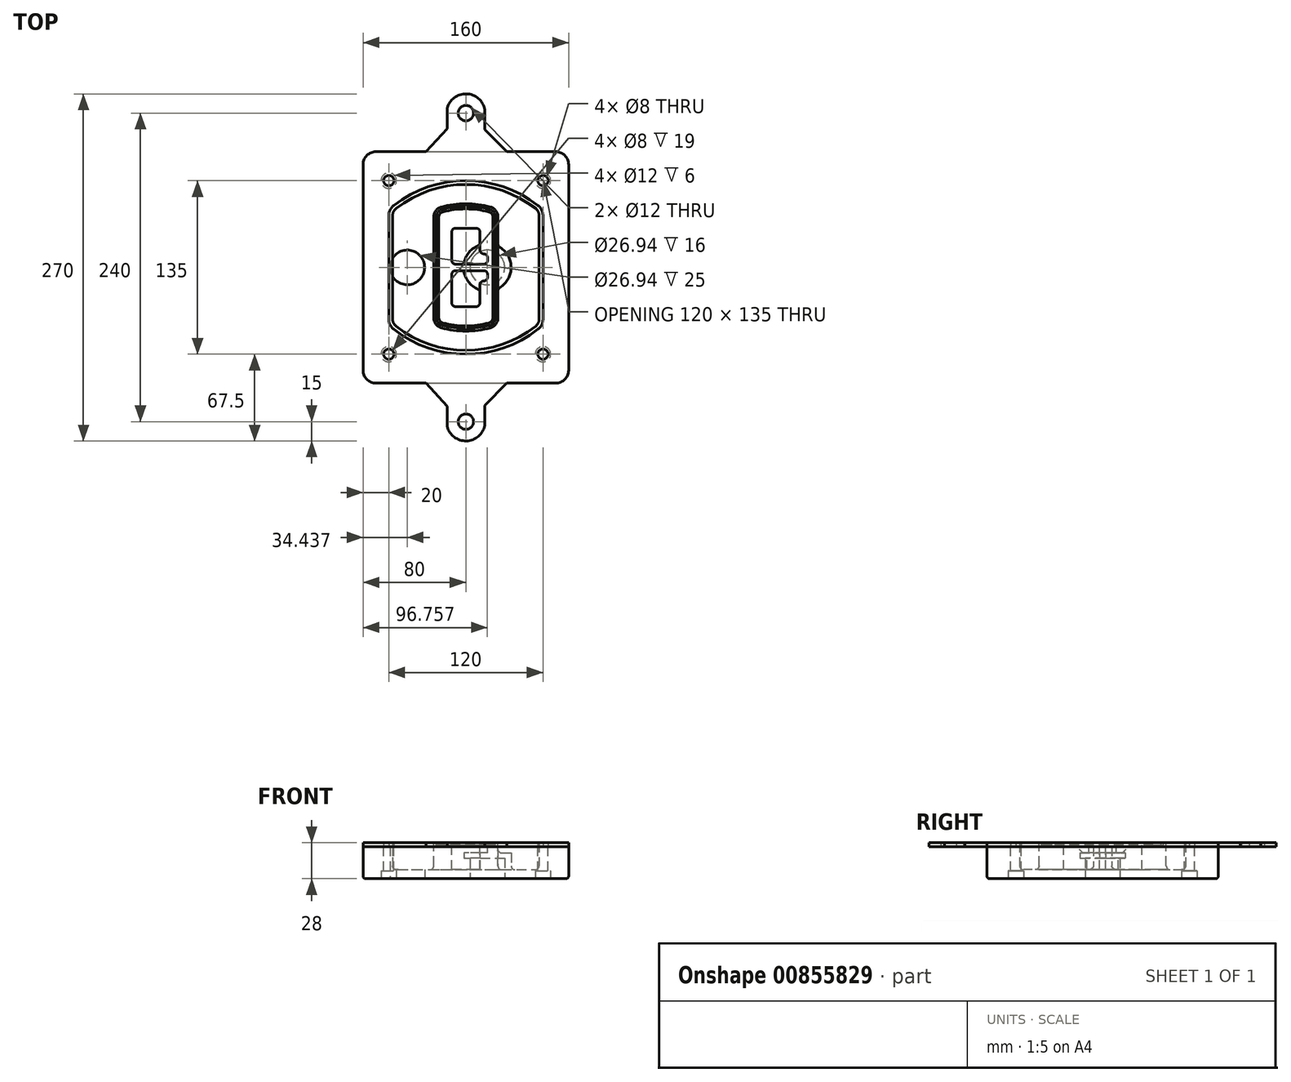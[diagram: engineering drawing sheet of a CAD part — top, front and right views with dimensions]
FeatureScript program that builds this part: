
annotation { "Feature Type Name" : "Feature", "Feature Type Description" : "" }
export const myFeature = defineFeature(function(context is Context, id is Id, definition is map)
    precondition{}
    {
        {
            var Q0;
            Q0=qCreatedBy(makeId("Top.planeOp"),FACE);
            var sketch = newSketch(context, id + "F0", { "sketchPlane" : qUnion([Q0])});
            skPoint(sketch, "E0.rect.middle", {"position": v(0, 0) * mm});
            skLineSegment(sketch, "E1.bottom", {"start": v(-70, -90) * mm, "end": v(70, -90) * mm});
            skLineSegment(sketch, "E1.top", {"start": v(-70, 90) * mm, "end": v(70, 90) * mm});
            skLineSegment(sketch, "E1.left", {"start": v(-80, -80) * mm, "end": v(-80, 80) * mm});
            skLineSegment(sketch, "E1.right", {"start": v(80, -80) * mm, "end": v(80, 80) * mm});
            skLineSegment(sketch, "E2", {"start": v(-80, 90) * mm, "end": v(80, -90) * mm, "construction": true});
            skLineSegment(sketch, "E3", {"start": v(80, 90) * mm, "end": v(-80, -90) * mm, "construction": true});
            skCircle(sketch, "E4", {"center": v(-60, 67.5) * mm, "radius": 4 * mm});
            skCircle(sketch, "E5", {"center": v(60, 67.5) * mm, "radius": 4 * mm});
            skCircle(sketch, "E6", {"center": v(60, -67.5) * mm, "radius": 4 * mm});
            skCircle(sketch, "E7", {"center": v(-60, -67.5) * mm, "radius": 4 * mm});
            skLineSegment(sketch, "E8", {"start": v(-60, 67.5) * mm, "end": v(60, 67.5) * mm, "construction": true});
            skLineSegment(sketch, "E9", {"start": v(60, 67.5) * mm, "end": v(60, -67.5) * mm, "construction": true});
            skLineSegment(sketch, "E10", {"start": v(60, -67.5) * mm, "end": v(-60, -67.5) * mm, "construction": true});
            skLineSegment(sketch, "E11", {"start": v(-60, -67.5) * mm, "end": v(-60, 67.5) * mm, "construction": true});
            skLineSegment(sketch, "E12", {"start": v(-60, 40.3) * mm, "end": v(-60, -40.3) * mm});
            skLineSegment(sketch, "E13", {"start": v(60, 40.3) * mm, "end": v(60, -40.3) * mm});
            skArc(sketch, "E14", {"start": v(56.15, 48.18) * mm, "mid": v(0, 67.5) * mm, "end": v(-56.15, 48.18) * mm});
            skArc(sketch, "E15", {"start": v(-56.15, -48.18) * mm, "mid": v(0, -67.5) * mm, "end": v(56.15, -48.18) * mm});
            skLineSegment(sketch, "E16", {"start": v(-60, 0) * mm, "end": v(60, 0) * mm, "construction": true});
            skPoint(sketch, "E17.visualSharp", {"position": v(-60, -45) * mm});
            skArc(sketch, "E17.filletArc", {"start": v(-60, -40.3) * mm, "mid": v(-58.99, -44.68) * mm, "end": v(-56.15, -48.18) * mm});
            skPoint(sketch, "E18.visualSharp", {"position": v(-60, 45) * mm});
            skArc(sketch, "E18.filletArc", {"start": v(-56.15, 48.18) * mm, "mid": v(-58.99, 44.68) * mm, "end": v(-60, 40.3) * mm});
            skPoint(sketch, "E19.visualSharp", {"position": v(60, 45) * mm});
            skArc(sketch, "E19.filletArc", {"start": v(60, 40.3) * mm, "mid": v(58.99, 44.68) * mm, "end": v(56.15, 48.18) * mm});
            skPoint(sketch, "E20.visualSharp", {"position": v(60, -45) * mm});
            skArc(sketch, "E20.filletArc", {"start": v(56.15, -48.18) * mm, "mid": v(58.99, -44.68) * mm, "end": v(60, -40.3) * mm});
            skPoint(sketch, "E21.visualSharp", {"position": v(-80, 90) * mm});
            skArc(sketch, "E21.filletArc", {"start": v(-70, 90) * mm, "mid": v(-77.07, 87.07) * mm, "end": v(-80, 80) * mm});
            skPoint(sketch, "E22.visualSharp", {"position": v(80, 90) * mm});
            skArc(sketch, "E22.filletArc", {"start": v(80, 80) * mm, "mid": v(77.07, 87.07) * mm, "end": v(70, 90) * mm});
            skPoint(sketch, "E23.visualSharp", {"position": v(80, -90) * mm});
            skArc(sketch, "E23.filletArc", {"start": v(70, -90) * mm, "mid": v(77.07, -87.07) * mm, "end": v(80, -80) * mm});
            skPoint(sketch, "E24.visualSharp", {"position": v(-80, -90) * mm});
            skArc(sketch, "E24.filletArc", {"start": v(-80, -80) * mm, "mid": v(-77.07, -87.07) * mm, "end": v(-70, -90) * mm});
            skArc(sketch, "E25.0", {"start": v(57, 40.3) * mm, "mid": v(56.3, 43.36) * mm, "end": v(54.3, 45.81) * mm});
            skLineSegment(sketch, "E25.1", {"start": v(57, 40.3) * mm, "end": v(57, -40.3) * mm});
            skArc(sketch, "E25.2", {"start": v(54.3, -45.81) * mm, "mid": v(56.3, -43.36) * mm, "end": v(57, -40.3) * mm});
            skArc(sketch, "E25.3", {"start": v(-54.3, -45.81) * mm, "mid": v(0, -64.5) * mm, "end": v(54.3, -45.81) * mm});
            skArc(sketch, "E25.4", {"start": v(-57, -40.3) * mm, "mid": v(-56.3, -43.36) * mm, "end": v(-54.3, -45.81) * mm});
            skArc(sketch, "E25.5", {"start": v(54.3, 45.81) * mm, "mid": v(0, 64.5) * mm, "end": v(-54.3, 45.81) * mm});
            skLineSegment(sketch, "E25.6", {"start": v(-57, 40.3) * mm, "end": v(-57, -40.3) * mm});
            skArc(sketch, "E25.7", {"start": v(-54.3, 45.81) * mm, "mid": v(-56.3, 43.36) * mm, "end": v(-57, 40.3) * mm});
            skArc(sketch, "E26.0", {"start": v(-58.62, 51.33) * mm, "mid": v(-62.58, 46.43) * mm, "end": v(-64, 40.3) * mm});
            skArc(sketch, "E26.1", {"start": v(58.62, 51.33) * mm, "mid": v(0, 71.5) * mm, "end": v(-58.62, 51.33) * mm});
            skArc(sketch, "E26.2", {"start": v(64, 40.3) * mm, "mid": v(62.58, 46.43) * mm, "end": v(58.62, 51.33) * mm});
            skLineSegment(sketch, "E26.3", {"start": v(64, 40.3) * mm, "end": v(64, -40.3) * mm});
            skArc(sketch, "E26.4", {"start": v(58.62, -51.33) * mm, "mid": v(62.58, -46.43) * mm, "end": v(64, -40.3) * mm});
            skLineSegment(sketch, "E26.5", {"start": v(-64, 40.3) * mm, "end": v(-64, -40.3) * mm});
            skArc(sketch, "E26.6", {"start": v(-58.62, -51.33) * mm, "mid": v(0, -71.5) * mm, "end": v(58.62, -51.33) * mm});
            skArc(sketch, "E26.7", {"start": v(-64, -40.3) * mm, "mid": v(-62.58, -46.43) * mm, "end": v(-58.62, -51.33) * mm});
            skSolve(sketch);
        }
        {
            var Q0;
            Q0=makeQuery(id+"F0.imprint","IMPRINT",FACE,{"disambiguationData":[TD([[makeQuery(id+"F0.imprint","IMPRINT",EDGE,{"derivedFrom":sQuery(id+"F0.wireOp",EDGE,"E1.bottom")}),1.0]])]});
            var Q1;
            Q1=makeQuery(id+"F0.imprint","IMPRINT",FACE,{"disambiguationData":[TD([[makeQuery(id+"F0.imprint","IMPRINT",EDGE,{"derivedFrom":sQuery(id+"F0.wireOp",EDGE,"E12")}),1.0]])]});
            var Q2;
            Q2=makeQuery(id+"F0.imprint","IMPRINT",FACE,{"disambiguationData":[TD([[makeQuery(id+"F0.imprint","IMPRINT",EDGE,{"derivedFrom":sQuery(id+"F0.wireOp",EDGE,"E25.0")}),1.0]])]});
            var Q3;
            Q3=makeQuery(id+"F0.imprint","IMPRINT",FACE,{"disambiguationData":[TD([[makeQuery(id+"F0.imprint","IMPRINT",EDGE,{"derivedFrom":sQuery(id+"F0.wireOp",EDGE,"E12")}),-1.0]])]});
            extrude(context, id + "F1", {"entities" : qUnion([Q0, Q1, Q2, Q3]), "oppositeDirection" : true, "depth" : 25 * mm});
        }
        {
            var Q0;
            Q0=makeQuery(id+"F0.imprint","IMPRINT",FACE,{"disambiguationData":[TD([[makeQuery(id+"F0.imprint","IMPRINT",EDGE,{"derivedFrom":sQuery(id+"F0.wireOp",EDGE,"E12")}),1.0]])]});
            extrude(context, id + "F2", {"entities" : qUnion([Q0]), "operationType" : NewBodyOperationType.ADD, "depth" : 3 * mm});
        }
        {
            var Q0;
            Q0=makeQuery(id+"F0.imprint","IMPRINT",FACE,{"disambiguationData":[TD([[makeQuery(id+"F0.imprint","IMPRINT",EDGE,{"derivedFrom":sQuery(id+"F0.wireOp",EDGE,"E25.0")}),1.0]])]});
            extrude(context, id + "F3", {"entities" : qUnion([Q0]), "operationType" : NewBodyOperationType.REMOVE, "oppositeDirection" : true, "depth" : 18 * mm});
        }
        {
            var Q0;
            Q0=makeQuery(id+"F2.opExtrude","CAP_FACE",FACE,{"disambiguationData":[OSD([sQuery(id+"F0.wireOp",EDGE,"E12"),sQuery(id+"F0.wireOp",EDGE,"E13"),sQuery(id+"F0.wireOp",EDGE,"E14"),sQuery(id+"F0.wireOp",EDGE,"E15"),sQuery(id+"F0.wireOp",EDGE,"E17.filletArc"),sQuery(id+"F0.wireOp",EDGE,"E18.filletArc"),sQuery(id+"F0.wireOp",EDGE,"E19.filletArc"),sQuery(id+"F0.wireOp",EDGE,"E20.filletArc"),sQuery(id+"F0.wireOp",EDGE,"E25.0"),sQuery(id+"F0.wireOp",EDGE,"E25.1"),sQuery(id+"F0.wireOp",EDGE,"E25.2"),sQuery(id+"F0.wireOp",EDGE,"E25.3"),sQuery(id+"F0.wireOp",EDGE,"E25.4"),sQuery(id+"F0.wireOp",EDGE,"E25.5"),sQuery(id+"F0.wireOp",EDGE,"E25.6"),sQuery(id+"F0.wireOp",EDGE,"E25.7")])],"isStart":false});
            var sketch = newSketch(context, id + "F4", { "sketchPlane" : qUnion([Q0])});
            skArc(sketch, "E27.0", {"start": v(-19.08, -46.97) * mm, "mid": v(0, -49.5) * mm, "end": v(19.08, -46.97) * mm});
            skArc(sketch, "E28.0", {"start": v(19.08, 46.97) * mm, "mid": v(0, 49.5) * mm, "end": v(-19.08, 46.97) * mm});
            skLineSegment(sketch, "E29", {"start": v(-25, 39.25) * mm, "end": v(-25, -39.25) * mm});
            skLineSegment(sketch, "E30", {"start": v(25, 39.25) * mm, "end": v(25, -39.25) * mm});
            skLineSegment(sketch, "E31", {"start": v(-25, 45.1) * mm, "end": v(25, 45.1) * mm, "construction": true});
            skLineSegment(sketch, "E32", {"start": v(-25, -45.1) * mm, "end": v(25, -45.1) * mm, "construction": true});
            skPoint(sketch, "E33.visualSharp", {"position": v(-25, 45.1) * mm});
            skArc(sketch, "E33.filletArc", {"start": v(-19.08, 46.97) * mm, "mid": v(-23.35, 44.11) * mm, "end": v(-25, 39.25) * mm});
            skPoint(sketch, "E34.visualSharp", {"position": v(25, 45.1) * mm});
            skArc(sketch, "E34.filletArc", {"start": v(25, 39.25) * mm, "mid": v(23.35, 44.11) * mm, "end": v(19.08, 46.97) * mm});
            skPoint(sketch, "E35.visualSharp", {"position": v(25, -45.1) * mm});
            skArc(sketch, "E35.filletArc", {"start": v(19.08, -46.97) * mm, "mid": v(23.35, -44.11) * mm, "end": v(25, -39.25) * mm});
            skPoint(sketch, "E36.visualSharp", {"position": v(-25, -45.1) * mm});
            skArc(sketch, "E36.filletArc", {"start": v(-25, -39.25) * mm, "mid": v(-23.35, -44.11) * mm, "end": v(-19.08, -46.97) * mm});
            skArc(sketch, "E37.0", {"start": v(54.3, 45.81) * mm, "mid": v(0, 64.5) * mm, "end": v(-54.3, 45.81) * mm});
            skArc(sketch, "E37.1", {"start": v(-54.3, 45.81) * mm, "mid": v(-56.3, 43.36) * mm, "end": v(-57, 40.3) * mm});
            skLineSegment(sketch, "E37.2", {"start": v(-57, 40.3) * mm, "end": v(-57, -40.3) * mm});
            skArc(sketch, "E37.3", {"start": v(-57, -40.3) * mm, "mid": v(-56.3, -43.36) * mm, "end": v(-54.3, -45.81) * mm});
            skArc(sketch, "E37.4", {"start": v(-54.3, -45.81) * mm, "mid": v(0, -64.5) * mm, "end": v(54.3, -45.81) * mm});
            skArc(sketch, "E37.5", {"start": v(54.3, -45.81) * mm, "mid": v(56.3, -43.36) * mm, "end": v(57, -40.3) * mm});
            skLineSegment(sketch, "E37.6", {"start": v(57, 40.3) * mm, "end": v(57, -40.3) * mm});
            skArc(sketch, "E37.7", {"start": v(57, 40.3) * mm, "mid": v(56.3, 43.36) * mm, "end": v(54.3, 45.81) * mm});
            skLineSegment(sketch, "E38.0", {"start": v(23, 39.25) * mm, "end": v(23, -39.25) * mm});
            skArc(sketch, "E38.1", {"start": v(18.56, -45.04) * mm, "mid": v(21.76, -42.9) * mm, "end": v(23, -39.25) * mm});
            skArc(sketch, "E38.2", {"start": v(-18.56, -45.04) * mm, "mid": v(0, -47.5) * mm, "end": v(18.56, -45.04) * mm});
            skArc(sketch, "E38.3", {"start": v(-23, -39.25) * mm, "mid": v(-21.76, -42.9) * mm, "end": v(-18.56, -45.04) * mm});
            skLineSegment(sketch, "E38.4", {"start": v(-23, 39.25) * mm, "end": v(-23, -39.25) * mm});
            skArc(sketch, "E38.5", {"start": v(23, 39.25) * mm, "mid": v(21.76, 42.9) * mm, "end": v(18.56, 45.04) * mm});
            skArc(sketch, "E38.6", {"start": v(-18.56, 45.04) * mm, "mid": v(-21.76, 42.9) * mm, "end": v(-23, 39.25) * mm});
            skArc(sketch, "E38.7", {"start": v(18.56, 45.04) * mm, "mid": v(0, 47.5) * mm, "end": v(-18.56, 45.04) * mm});
            skArc(sketch, "E39.0", {"start": v(21, 39.25) * mm, "mid": v(20.18, 41.68) * mm, "end": v(18.04, 43.1) * mm});
            skLineSegment(sketch, "E39.1", {"start": v(21, 39.25) * mm, "end": v(21, -39.25) * mm});
            skArc(sketch, "E39.2", {"start": v(18.04, -43.1) * mm, "mid": v(20.18, -41.68) * mm, "end": v(21, -39.25) * mm});
            skArc(sketch, "E39.3", {"start": v(-18.04, -43.1) * mm, "mid": v(0, -45.5) * mm, "end": v(18.04, -43.1) * mm});
            skArc(sketch, "E39.4", {"start": v(-21, -39.25) * mm, "mid": v(-20.18, -41.68) * mm, "end": v(-18.04, -43.1) * mm});
            skArc(sketch, "E39.5", {"start": v(18.04, 43.1) * mm, "mid": v(0, 45.5) * mm, "end": v(-18.04, 43.1) * mm});
            skLineSegment(sketch, "E39.6", {"start": v(-21, 39.25) * mm, "end": v(-21, -39.25) * mm});
            skArc(sketch, "E39.7", {"start": v(-18.04, 43.1) * mm, "mid": v(-20.18, 41.68) * mm, "end": v(-21, 39.25) * mm});
            skLineSegment(sketch, "E40", {"start": v(-25, 0) * mm, "end": v(25, 0) * mm, "construction": true});
            skLineSegment(sketch, "E41", {"start": v(-11, 5.5) * mm, "end": v(-11, 27.5) * mm});
            skLineSegment(sketch, "E42", {"start": v(-8, 30.5) * mm, "end": v(8, 30.5) * mm});
            skLineSegment(sketch, "E43", {"start": v(11, 27.5) * mm, "end": v(11, 13.5) * mm});
            skLineSegment(sketch, "E44", {"start": v(14, 10.5) * mm, "end": v(14, 10.5) * mm});
            skLineSegment(sketch, "E45", {"start": v(17, 7.5) * mm, "end": v(17, 5.5) * mm});
            skLineSegment(sketch, "E46", {"start": v(14, 2.5) * mm, "end": v(-8, 2.5) * mm});
            skPoint(sketch, "E47.visualSharp", {"position": v(-11, 30.5) * mm});
            skArc(sketch, "E47.filletArc", {"start": v(-8, 30.5) * mm, "mid": v(-10.12, 29.62) * mm, "end": v(-11, 27.5) * mm});
            skPoint(sketch, "E48.visualSharp", {"position": v(11, 30.5) * mm});
            skArc(sketch, "E48.filletArc", {"start": v(11, 27.5) * mm, "mid": v(10.12, 29.62) * mm, "end": v(8, 30.5) * mm});
            skPoint(sketch, "E49.visualSharp", {"position": v(11, 10.5) * mm});
            skArc(sketch, "E49.filletArc", {"start": v(11, 13.5) * mm, "mid": v(11.88, 11.38) * mm, "end": v(14, 10.5) * mm});
            skPoint(sketch, "E50.visualSharp", {"position": v(17, 10.5) * mm});
            skArc(sketch, "E50.filletArc", {"start": v(17, 7.5) * mm, "mid": v(16.12, 9.62) * mm, "end": v(14, 10.5) * mm});
            skPoint(sketch, "E51.visualSharp", {"position": v(17, 2.5) * mm});
            skArc(sketch, "E51.filletArc", {"start": v(14, 2.5) * mm, "mid": v(16.12, 3.38) * mm, "end": v(17, 5.5) * mm});
            skPoint(sketch, "E52.visualSharp", {"position": v(-11, 2.5) * mm});
            skArc(sketch, "E52.filletArc", {"start": v(-11, 5.5) * mm, "mid": v(-10.12, 3.38) * mm, "end": v(-8, 2.5) * mm});
            skLineSegment(sketch, "E53.0.MirrorCS", {"start": v(14, -2.5) * mm, "end": v(-8, -2.5) * mm});
            skArc(sketch, "E54.0.MirrorCS", {"start": v(-11, -5.5) * mm, "mid": v(-10.12, -3.38) * mm, "end": v(-8, -2.5) * mm});
            skLineSegment(sketch, "E55.0.MirrorCS", {"start": v(-11, -5.5) * mm, "end": v(-11, -27.5) * mm});
            skArc(sketch, "E56.0.MirrorCS", {"start": v(-8, -30.5) * mm, "mid": v(-10.12, -29.62) * mm, "end": v(-11, -27.5) * mm});
            skLineSegment(sketch, "E57.0.MirrorCS", {"start": v(-8, -30.5) * mm, "end": v(8, -30.5) * mm});
            skArc(sketch, "E58.0.MirrorCS", {"start": v(11, -27.5) * mm, "mid": v(10.12, -29.62) * mm, "end": v(8, -30.5) * mm});
            skLineSegment(sketch, "E59.0.MirrorCS", {"start": v(11, -27.5) * mm, "end": v(11, -13.5) * mm});
            skArc(sketch, "E60.0.MirrorCS", {"start": v(11, -13.5) * mm, "mid": v(11.88, -11.38) * mm, "end": v(14, -10.5) * mm});
            skArc(sketch, "E61.0.MirrorCS", {"start": v(17, -7.5) * mm, "mid": v(16.12, -9.62) * mm, "end": v(14, -10.5) * mm});
            skLineSegment(sketch, "E62.0.MirrorCS", {"start": v(17, -7.5) * mm, "end": v(17, -5.5) * mm});
            skArc(sketch, "E63.0.MirrorCS", {"start": v(14, -2.5) * mm, "mid": v(16.12, -3.38) * mm, "end": v(17, -5.5) * mm});
            skSolve(sketch);
        }
        {
            var Q0;
            Q0=makeQuery(id+"F4.imprint","IMPRINT",FACE,{"disambiguationData":[TD([[makeQuery(id+"F4.imprint","IMPRINT",EDGE,{"derivedFrom":sQuery(id+"F4.wireOp",EDGE,"E27.0")}),1.0]])]});
            var Q1;
            Q1=makeQuery(id+"F4.imprint","IMPRINT",FACE,{"disambiguationData":[TD([[makeQuery(id+"F4.imprint","IMPRINT",EDGE,{"derivedFrom":sQuery(id+"F4.wireOp",EDGE,"E38.0")}),-1.0]])]});
            var Q2;
            Q2=makeQuery(id+"F4.imprint","IMPRINT",FACE,{"disambiguationData":[TD([[makeQuery(id+"F4.imprint","IMPRINT",EDGE,{"derivedFrom":sQuery(id+"F4.wireOp",EDGE,"E39.0")}),1.0]])]});
            extrude(context, id + "F5", {"entities" : qUnion([Q0, Q1, Q2]), "operationType" : NewBodyOperationType.ADD, "endBound" : BoundingType.UP_TO_NEXT, "oppositeDirection" : true, "depth" : 25 * mm});
        }
        {
            var Q0;
            Q0=makeQuery(id+"F4.imprint","IMPRINT",FACE,{"disambiguationData":[TD([[makeQuery(id+"F4.imprint","IMPRINT",EDGE,{"derivedFrom":sQuery(id+"F4.wireOp",EDGE,"E38.0")}),-1.0]])]});
            extrude(context, id + "F6", {"entities" : qUnion([Q0]), "operationType" : NewBodyOperationType.REMOVE, "oppositeDirection" : true, "depth" : 2 * mm});
        }
        {
            var Q0;
            Q0=makeQuery(id+"F1.opExtrude","CAP_FACE",FACE,{"disambiguationData":[OSD([sQuery(id+"F0.wireOp",EDGE,"E1.bottom"),sQuery(id+"F0.wireOp",EDGE,"E1.top"),sQuery(id+"F0.wireOp",EDGE,"E1.left"),sQuery(id+"F0.wireOp",EDGE,"E1.right"),sQuery(id+"F0.wireOp",EDGE,"E4"),sQuery(id+"F0.wireOp",EDGE,"E5"),sQuery(id+"F0.wireOp",EDGE,"E6"),sQuery(id+"F0.wireOp",EDGE,"E7"),sQuery(id+"F0.wireOp",EDGE,"E21.filletArc"),sQuery(id+"F0.wireOp",EDGE,"E22.filletArc"),sQuery(id+"F0.wireOp",EDGE,"E23.filletArc"),sQuery(id+"F0.wireOp",EDGE,"E24.filletArc")])],"isStart":false});
            var sketch = newSketch(context, id + "F7", { "sketchPlane" : qUnion([Q0])});
            skCircle(sketch, "E64", {"center": v(16.76, 0) * mm, "radius": 13.47 * mm});
            skCircle(sketch, "E65", {"center": v(-45.56, 0) * mm, "radius": 13.47 * mm});
            skLineSegment(sketch, "E66", {"start": v(80, 0) * mm, "end": v(-80, 0) * mm});
            skCircle(sketch, "E67", {"center": v(16.76, 0) * mm, "radius": 18.47 * mm});
            skCircle(sketch, "E68", {"center": v(60, -67.5) * mm, "radius": 6 * mm});
            skCircle(sketch, "E69", {"center": v(-60, -67.5) * mm, "radius": 6 * mm});
            skCircle(sketch, "E70", {"center": v(-60, 67.5) * mm, "radius": 6 * mm});
            skCircle(sketch, "E71", {"center": v(60, 67.5) * mm, "radius": 6 * mm});
            skSolve(sketch);
        }
        {
            var Q0;
            {var subQ1=sQuery(id+"F7.wireOp",EDGE,"E66");var subQ4=sQuery(id+"F7.wireOp",EDGE,"E64");var subQ6=makeQuery(id+"F7.imprint","INTERSECT",VERTEX,{"disambiguationData":[OD(0.0)],"derivedFrom":[subQ4,subQ1]});Q0=makeQuery(id+"F7.imprint","IMPRINT",FACE,{"disambiguationData":[TD([[makeQuery(id+"F7.imprint","IMPRINT",EDGE,{"disambiguationData":[TD([[subQ6,-1.0]])],"derivedFrom":subQ4}),-1.0]])]});}
            var Q1;
            {var subQ0=sQuery(id+"F7.wireOp",EDGE,"E66");var subQ1=sQuery(id+"F7.wireOp",EDGE,"E64");var subQ3=makeQuery(id+"F7.imprint","INTERSECT",VERTEX,{"disambiguationData":[OD(0.0)],"derivedFrom":[subQ1,subQ0]});Q1=makeQuery(id+"F7.imprint","IMPRINT",FACE,{"disambiguationData":[TD([[makeQuery(id+"F7.imprint","IMPRINT",EDGE,{"disambiguationData":[TD([[subQ3,-1.0]])],"derivedFrom":subQ1}),1.0]])]});}
            var Q2;
            {var subQ0=sQuery(id+"F7.wireOp",EDGE,"E66");var subQ1=sQuery(id+"F7.wireOp",EDGE,"E64");var subQ3=makeQuery(id+"F7.imprint","INTERSECT",VERTEX,{"disambiguationData":[OD(0.0)],"derivedFrom":[subQ1,subQ0]});Q2=makeQuery(id+"F7.imprint","IMPRINT",FACE,{"disambiguationData":[TD([[makeQuery(id+"F7.imprint","IMPRINT",EDGE,{"disambiguationData":[TD([[subQ3,1.0]])],"derivedFrom":subQ1}),1.0]])]});}
            var Q3;
            {var subQ1=sQuery(id+"F7.wireOp",EDGE,"E66");var subQ4=sQuery(id+"F7.wireOp",EDGE,"E64");var subQ6=makeQuery(id+"F7.imprint","INTERSECT",VERTEX,{"disambiguationData":[OD(0.0)],"derivedFrom":[subQ4,subQ1]});Q3=makeQuery(id+"F7.imprint","IMPRINT",FACE,{"disambiguationData":[TD([[makeQuery(id+"F7.imprint","IMPRINT",EDGE,{"disambiguationData":[TD([[subQ6,1.0]])],"derivedFrom":subQ4}),-1.0]])]});}
            extrude(context, id + "F8", {"entities" : qUnion([Q0, Q1, Q2, Q3]), "operationType" : NewBodyOperationType.ADD, "oppositeDirection" : true, "depth" : 20 * mm});
        }
        {
            var Q0;
            {var subQ0=sQuery(id+"F7.wireOp",EDGE,"E66");var subQ1=sQuery(id+"F7.wireOp",EDGE,"E64");var subQ3=makeQuery(id+"F7.imprint","INTERSECT",VERTEX,{"disambiguationData":[OD(0.0)],"derivedFrom":[subQ1,subQ0]});Q0=makeQuery(id+"F7.imprint","IMPRINT",FACE,{"disambiguationData":[TD([[makeQuery(id+"F7.imprint","IMPRINT",EDGE,{"disambiguationData":[TD([[subQ3,-1.0]])],"derivedFrom":subQ1}),1.0]])]});}
            var Q1;
            {var subQ0=sQuery(id+"F7.wireOp",EDGE,"E66");var subQ1=sQuery(id+"F7.wireOp",EDGE,"E64");var subQ3=makeQuery(id+"F7.imprint","INTERSECT",VERTEX,{"disambiguationData":[OD(0.0)],"derivedFrom":[subQ1,subQ0]});Q1=makeQuery(id+"F7.imprint","IMPRINT",FACE,{"disambiguationData":[TD([[makeQuery(id+"F7.imprint","IMPRINT",EDGE,{"disambiguationData":[TD([[subQ3,1.0]])],"derivedFrom":subQ1}),1.0]])]});}
            extrude(context, id + "F9", {"entities" : qUnion([Q0, Q1]), "operationType" : NewBodyOperationType.REMOVE, "oppositeDirection" : true, "depth" : 16 * mm});
        }
        {
            var Q0;
            {var subQ0=sQuery(id+"F7.wireOp",EDGE,"E66");var subQ1=sQuery(id+"F7.wireOp",EDGE,"E65");var subQ3=makeQuery(id+"F7.imprint","INTERSECT",VERTEX,{"disambiguationData":[OD(0.0)],"derivedFrom":[subQ1,subQ0]});Q0=makeQuery(id+"F7.imprint","IMPRINT",FACE,{"disambiguationData":[TD([[makeQuery(id+"F7.imprint","IMPRINT",EDGE,{"disambiguationData":[TD([[subQ3,-1.0]])],"derivedFrom":subQ1}),1.0]])]});}
            var Q1;
            {var subQ0=sQuery(id+"F7.wireOp",EDGE,"E66");var subQ1=sQuery(id+"F7.wireOp",EDGE,"E65");var subQ3=makeQuery(id+"F7.imprint","INTERSECT",VERTEX,{"disambiguationData":[OD(0.0)],"derivedFrom":[subQ1,subQ0]});Q1=makeQuery(id+"F7.imprint","IMPRINT",FACE,{"disambiguationData":[TD([[makeQuery(id+"F7.imprint","IMPRINT",EDGE,{"disambiguationData":[TD([[subQ3,1.0]])],"derivedFrom":subQ1}),1.0]])]});}
            extrude(context, id + "F10", {"entities" : qUnion([Q0, Q1]), "operationType" : NewBodyOperationType.REMOVE, "oppositeDirection" : true, "depth" : 25 * mm});
        }
        {
            var Q0;
            Q0=makeQuery(id+"F7.imprint","IMPRINT",FACE,{"disambiguationData":[TD([[makeQuery(id+"F7.imprint","IMPRINT",EDGE,{"derivedFrom":sQuery(id+"F7.wireOp",EDGE,"E68")}),1.0]])]});
            var Q1;
            Q1=makeQuery(id+"F7.imprint","IMPRINT",FACE,{"disambiguationData":[TD([[makeQuery(id+"F7.imprint","IMPRINT",EDGE,{"derivedFrom":makeQuery(id+"F1.opExtrude","CAP_EDGE",EDGE,{"disambiguationData":[OSD([sQuery(id+"F0.wireOp",EDGE,"E5")])],"isStart":false})}),-1.0]])]});
            var Q2;
            Q2=makeQuery(id+"F7.imprint","IMPRINT",FACE,{"disambiguationData":[TD([[makeQuery(id+"F7.imprint","IMPRINT",EDGE,{"derivedFrom":sQuery(id+"F7.wireOp",EDGE,"E69")}),1.0]])]});
            var Q3;
            Q3=makeQuery(id+"F7.imprint","IMPRINT",FACE,{"disambiguationData":[TD([[makeQuery(id+"F7.imprint","IMPRINT",EDGE,{"derivedFrom":makeQuery(id+"F1.opExtrude","CAP_EDGE",EDGE,{"disambiguationData":[OSD([sQuery(id+"F0.wireOp",EDGE,"E4")])],"isStart":false})}),-1.0]])]});
            var Q4;
            Q4=makeQuery(id+"F7.imprint","IMPRINT",FACE,{"disambiguationData":[TD([[makeQuery(id+"F7.imprint","IMPRINT",EDGE,{"derivedFrom":sQuery(id+"F7.wireOp",EDGE,"E70")}),1.0]])]});
            var Q5;
            Q5=makeQuery(id+"F7.imprint","IMPRINT",FACE,{"disambiguationData":[TD([[makeQuery(id+"F7.imprint","IMPRINT",EDGE,{"derivedFrom":makeQuery(id+"F1.opExtrude","CAP_EDGE",EDGE,{"disambiguationData":[OSD([sQuery(id+"F0.wireOp",EDGE,"E7")])],"isStart":false})}),-1.0]])]});
            var Q6;
            Q6=makeQuery(id+"F7.imprint","IMPRINT",FACE,{"disambiguationData":[TD([[makeQuery(id+"F7.imprint","IMPRINT",EDGE,{"derivedFrom":sQuery(id+"F7.wireOp",EDGE,"E71")}),1.0]])]});
            var Q7;
            Q7=makeQuery(id+"F7.imprint","IMPRINT",FACE,{"disambiguationData":[TD([[makeQuery(id+"F7.imprint","IMPRINT",EDGE,{"derivedFrom":makeQuery(id+"F1.opExtrude","CAP_EDGE",EDGE,{"disambiguationData":[OSD([sQuery(id+"F0.wireOp",EDGE,"E6")])],"isStart":false})}),-1.0]])]});
            extrude(context, id + "F11", {"entities" : qUnion([Q0, Q1, Q2, Q3, Q4, Q5, Q6, Q7]), "operationType" : NewBodyOperationType.REMOVE, "oppositeDirection" : true, "depth" : 6 * mm});
        }
        {
            var Q0;
            Q0=makeQuery(id+"F9.boolean.opBoolean","COPY",FACE,{"derivedFrom":makeQuery(id+"F9.opExtrude","CAP_FACE",FACE,{"disambiguationData":[OSD([sQuery(id+"F7.wireOp",EDGE,"E64")])],"isStart":false})});
            var sketch = newSketch(context, id + "F12", { "sketchPlane" : qUnion([Q0])});
            skArc(sketch, "E72.0", {"start": v(11, 17.55) * mm, "mid": v(2.57, 11.82) * mm, "end": v(-1.54, 2.5) * mm});
            skArc(sketch, "E72.1", {"start": v(-1.54, -2.5) * mm, "mid": v(2.57, -11.82) * mm, "end": v(11, -17.55) * mm});
            skLineSegment(sketch, "E73", {"start": v(-1.54, -2.5) * mm, "end": v(14, -2.5) * mm});
            skLineSegment(sketch, "E74.0", {"start": v(14, 2.5) * mm, "end": v(-1.54, 2.5) * mm});
            skArc(sketch, "E74.1", {"start": v(14, 2.5) * mm, "mid": v(16.12, 3.38) * mm, "end": v(17, 5.5) * mm});
            skLineSegment(sketch, "E74.2", {"start": v(17, 7.5) * mm, "end": v(17, 5.5) * mm});
            skArc(sketch, "E74.3", {"start": v(17, 7.5) * mm, "mid": v(16.12, 9.62) * mm, "end": v(14, 10.5) * mm});
            skArc(sketch, "E74.4", {"start": v(11, 13.5) * mm, "mid": v(11.88, 11.38) * mm, "end": v(14, 10.5) * mm});
            skLineSegment(sketch, "E74.5", {"start": v(11, 17.55) * mm, "end": v(11, 13.5) * mm});
            skLineSegment(sketch, "E74.7", {"start": v(14, -2.5) * mm, "end": v(-1.54, -2.5) * mm});
            skArc(sketch, "E74.8", {"start": v(14, -2.5) * mm, "mid": v(16.12, -3.38) * mm, "end": v(17, -5.5) * mm});
            skLineSegment(sketch, "E74.9", {"start": v(17, -7.5) * mm, "end": v(17, -5.5) * mm});
            skArc(sketch, "E74.10", {"start": v(17, -7.5) * mm, "mid": v(16.12, -9.62) * mm, "end": v(14, -10.5) * mm});
            skArc(sketch, "E74.11", {"start": v(11, -13.5) * mm, "mid": v(11.88, -11.38) * mm, "end": v(14, -10.5) * mm});
            skLineSegment(sketch, "E74.12", {"start": v(11, -17.55) * mm, "end": v(11, -13.5) * mm});
            skPoint(sketch, "E75.orphan", {"position": v(11, -27.5) * mm});
            skPoint(sketch, "E76.orphan", {"position": v(-8, -2.5) * mm});
            skPoint(sketch, "E77.orphan", {"position": v(-8, 2.5) * mm});
            skPoint(sketch, "E78.orphan", {"position": v(11, 27.5) * mm});
            skSolve(sketch);
        }
        {
            var Q0;
            {var subQ7=sQuery(id+"F12.wireOp",EDGE,"E72.0");var subQ14=sQuery(id+"F12.wireOp",EDGE,"E72.1");var subQ16=sQuery(id+"F12.wireOp",EDGE,"E74.1");var subQ18=sQuery(id+"F12.wireOp",EDGE,"E74.8");Q0=qUnion([makeQuery(id+"F12.imprint","IMPRINT",FACE,{"disambiguationData":[TD([[makeQuery(id+"F12.imprint","IMPRINT",EDGE,{"derivedFrom":subQ7}),1.0]])]}),makeQuery(id+"F12.imprint","IMPRINT",FACE,{"disambiguationData":[TD([[makeQuery(id+"F12.imprint","IMPRINT",EDGE,{"derivedFrom":subQ14}),1.0]])]}),makeQuery(id+"F12.imprint","IMPRINT",FACE,{"disambiguationData":[TD([[makeQuery(id+"F12.imprint","IMPRINT",EDGE,{"derivedFrom":subQ16}),1.0]])]}),makeQuery(id+"F12.imprint","IMPRINT",FACE,{"disambiguationData":[TD([[makeQuery(id+"F12.imprint","IMPRINT",EDGE,{"derivedFrom":subQ18}),-1.0]])]})]);}
            var Q1;
            Q1=makeQuery(id+"F5.boolean.opBoolean","SPLIT",FACE,{"disambiguationData":[TD([makeQuery(id+"F5.opExtrude","SWEPT_FACE",FACE,{"disambiguationData":[OSD([sQuery(id+"F4.wireOp",EDGE,"E41")])]})])],"derivedFrom":makeQuery(id+"F3.boolean.opBoolean","COPY",FACE,{"derivedFrom":makeQuery(id+"F3.opExtrude","CAP_FACE",FACE,{"disambiguationData":[OSD([sQuery(id+"F0.wireOp",EDGE,"E25.0"),sQuery(id+"F0.wireOp",EDGE,"E25.1"),sQuery(id+"F0.wireOp",EDGE,"E25.2"),sQuery(id+"F0.wireOp",EDGE,"E25.3"),sQuery(id+"F0.wireOp",EDGE,"E25.4"),sQuery(id+"F0.wireOp",EDGE,"E25.5"),sQuery(id+"F0.wireOp",EDGE,"E25.6"),sQuery(id+"F0.wireOp",EDGE,"E25.7")])],"isStart":false})})});
            extrude(context, id + "F13", {"entities" : qUnion([Q0]), "operationType" : NewBodyOperationType.REMOVE, "endBound" : BoundingType.UP_TO_SURFACE, "endBoundEntityFace" : qUnion([Q1]), "depth" : 25 * mm});
        }
        {
            var Q0;
            Q0=makeQuery(id+"F3.boolean.opBoolean","COPY",EDGE,{"derivedFrom":makeQuery(id+"F3.opExtrude","CAP_EDGE",EDGE,{"disambiguationData":[OSD([sQuery(id+"F0.wireOp",EDGE,"E25.6")])],"isStart":false})});
            var Q1;
            Q1=makeQuery(id+"F8.boolean.opBoolean","INTERSECT",EDGE,{"derivedFrom":[makeQuery(id+"F5.opExtrude","SWEPT_FACE",FACE,{"disambiguationData":[OSD([sQuery(id+"F4.wireOp",EDGE,"E30")])]}),makeQuery(id+"F8.opExtrude","CAP_FACE",FACE,{"disambiguationData":[OSD([sQuery(id+"F7.wireOp",EDGE,"E67")])],"isStart":false})]});
            var Q2;
            Q2=makeQuery(id+"F8.boolean.opBoolean","INTERSECT",EDGE,{"disambiguationData":[OD(1.0)],"derivedFrom":[makeQuery(id+"F5.opExtrude","SWEPT_FACE",FACE,{"disambiguationData":[OSD([sQuery(id+"F4.wireOp",EDGE,"E30")])]}),makeQuery(id+"F8.opExtrude","SWEPT_FACE",FACE,{"disambiguationData":[OSD([sQuery(id+"F7.wireOp",EDGE,"E67")])]})]});
            var Q3;
            {var subQ0=sQuery(id+"F4.wireOp",EDGE,"E30");Q3=makeQuery(id+"F8.boolean.opBoolean","SPLIT",EDGE,{"disambiguationData":[TD([makeQuery(id+"F5.opExtrude","SWEPT_FACE",FACE,{"disambiguationData":[OSD([sQuery(id+"F4.wireOp",EDGE,"E35.filletArc")])]})])],"derivedFrom":makeQuery(id+"F5.opExtrude","CAP_EDGE",EDGE,{"disambiguationData":[OSD([subQ0])],"isStart":false})});}
            var Q4;
            {var subQ0=sQuery(id+"F0.wireOp",EDGE,"E25.7");var subQ1=sQuery(id+"F0.wireOp",EDGE,"E25.1");var subQ2=sQuery(id+"F0.wireOp",EDGE,"E25.6");var subQ3=sQuery(id+"F0.wireOp",EDGE,"E25.5");var subQ4=sQuery(id+"F0.wireOp",EDGE,"E25.4");var subQ5=sQuery(id+"F0.wireOp",EDGE,"E25.0");var subQ6=sQuery(id+"F0.wireOp",EDGE,"E25.2");var subQ7=sQuery(id+"F0.wireOp",EDGE,"E25.3");Q4=makeQuery(id+"F8.boolean.opBoolean","INTERSECT",EDGE,{"derivedFrom":[makeQuery(id+"F5.boolean.opBoolean","SPLIT",FACE,{"disambiguationData":[TD([makeQuery(id+"F2.opExtrude","SWEPT_FACE",FACE,{"disambiguationData":[OSD([subQ5])]})])],"derivedFrom":makeQuery(id+"F3.boolean.opBoolean","COPY",FACE,{"derivedFrom":makeQuery(id+"F3.opExtrude","CAP_FACE",FACE,{"disambiguationData":[OSD([subQ5,subQ1,subQ6,subQ7,subQ4,subQ3,subQ2,subQ0])],"isStart":false})})}),makeQuery(id+"F8.opExtrude","SWEPT_FACE",FACE,{"disambiguationData":[OSD([sQuery(id+"F7.wireOp",EDGE,"E67")])]})]});}
            var Q5;
            Q5=makeQuery(id+"F8.boolean.opBoolean","INTERSECT",EDGE,{"disambiguationData":[OD(0.0)],"derivedFrom":[makeQuery(id+"F5.opExtrude","SWEPT_FACE",FACE,{"disambiguationData":[OSD([sQuery(id+"F4.wireOp",EDGE,"E30")])]}),makeQuery(id+"F8.opExtrude","SWEPT_FACE",FACE,{"disambiguationData":[OSD([sQuery(id+"F7.wireOp",EDGE,"E67")])]})]});
            fillet(context, id + "F14", {"entities" : qUnion([Q0, Q1, Q2, Q3, Q4, Q5]), "radius" : 3 * mm, "tangentPropagation" : true, "allowEdgeOverflow" : false});
        }
        {
            var Q0;
            Q0=makeQuery(id+"F1.opExtrude","CAP_EDGE",EDGE,{"disambiguationData":[OSD([sQuery(id+"F0.wireOp",EDGE,"E1.bottom")])],"isStart":false});
            fillet(context, id + "F15", {"entities" : qUnion([Q0]), "radius" : 2 * mm, "tangentPropagation" : true, "allowEdgeOverflow" : false});
        }
        {
            var Q0;
            {var subQ0=sQuery(id+"F0.wireOp",EDGE,"E21.filletArc");var subQ1=sQuery(id+"F0.wireOp",EDGE,"E7");var subQ2=sQuery(id+"F0.wireOp",EDGE,"E6");var subQ3=sQuery(id+"F0.wireOp",EDGE,"E5");var subQ4=sQuery(id+"F0.wireOp",EDGE,"E4");var subQ5=sQuery(id+"F0.wireOp",EDGE,"E22.filletArc");var subQ6=sQuery(id+"F0.wireOp",EDGE,"E1.bottom");var subQ7=sQuery(id+"F0.wireOp",EDGE,"E1.right");var subQ8=sQuery(id+"F0.wireOp",EDGE,"E1.top");var subQ9=sQuery(id+"F0.wireOp",EDGE,"E1.left");var subQ10=sQuery(id+"F0.wireOp",EDGE,"E23.filletArc");var subQ11=sQuery(id+"F0.wireOp",EDGE,"E24.filletArc");Q0=makeQuery(id+"F2.boolean.opBoolean","SPLIT",FACE,{"disambiguationData":[TD([makeQuery(id+"F1.opExtrude","SWEPT_FACE",FACE,{"disambiguationData":[OSD([subQ6])]})])],"derivedFrom":makeQuery(id+"F1.opExtrude","CAP_FACE",FACE,{"disambiguationData":[OSD([subQ6,subQ8,subQ9,subQ7,subQ4,subQ3,subQ2,subQ1,subQ0,subQ5,subQ10,subQ11])],"isStart":true})});}
            var sketch = newSketch(context, id + "F16", { "sketchPlane" : qUnion([Q0])});
            skLineSegment(sketch, "E79", {"start": v(0, 90) * mm, "end": v(0, 120) * mm, "construction": true});
            skCircle(sketch, "E80", {"center": v(0, 120) * mm, "radius": 6 * mm});
            skLineSegment(sketch, "E81", {"start": v(14.72, 107.25) * mm, "end": v(14.72, 122.9) * mm});
            skLineSegment(sketch, "E82", {"start": v(-14.55, 108) * mm, "end": v(-14.55, 123.66) * mm});
            skArc(sketch, "E83", {"start": v(14.72, 122.9) * mm, "mid": v(0.38, 135) * mm, "end": v(-14.55, 123.66) * mm});
            skLineSegment(sketch, "E84", {"start": v(-14.55, 108) * mm, "end": v(-31.01, 90) * mm});
            skLineSegment(sketch, "E85", {"start": v(14.72, 107.25) * mm, "end": v(31.96, 90) * mm});
            skLineSegment(sketch, "E86", {"start": v(-80, 0) * mm, "end": v(80, 0) * mm, "construction": true});
            skLineSegment(sketch, "E87", {"start": v(-31.01, 90) * mm, "end": v(31.96, 90) * mm});
            skLineSegment(sketch, "E88.MirrorCS", {"start": v(-14.55, -108) * mm, "end": v(-31.01, -90) * mm});
            skLineSegment(sketch, "E89.MirrorCS", {"start": v(14.72, -107.25) * mm, "end": v(14.72, -122.9) * mm});
            skLineSegment(sketch, "E90.MirrorCS", {"start": v(-31.01, -90) * mm, "end": v(31.96, -90) * mm});
            skLineSegment(sketch, "E91.MirrorCS", {"start": v(-14.55, -108) * mm, "end": v(-14.55, -123.66) * mm});
            skCircle(sketch, "E92.MirrorC", {"center": v(0, -120) * mm, "radius": 6 * mm});
            skArc(sketch, "E93.MirrorCS", {"start": v(14.72, -122.9) * mm, "mid": v(0.38, -135) * mm, "end": v(-14.55, -123.66) * mm});
            skLineSegment(sketch, "E94.MirrorCS", {"start": v(14.72, -107.25) * mm, "end": v(31.96, -90) * mm});
            skLineSegment(sketch, "E95.MirrorCS", {"start": v(0, -90) * mm, "end": v(0, -120) * mm, "construction": true});
            skSolve(sketch);
        }
        {
            var Q0;
            {var subQ5=sQuery(id+"F16.wireOp",EDGE,"E87");Q0=makeQuery(id+"F16.imprint","IMPRINT",FACE,{"disambiguationData":[TD([[makeQuery(id+"F16.imprint","IMPRINT",EDGE,{"derivedFrom":subQ5}),-1.0]])]});}
            var Q1;
            Q1=makeQuery(id+"F16.imprint","IMPRINT",FACE,{"disambiguationData":[TD([[makeQuery(id+"F16.imprint","IMPRINT",EDGE,{"derivedFrom":sQuery(id+"F16.wireOp",EDGE,"E80")}),-1.0]])]});
            var Q2;
            Q2=makeQuery(id+"F16.imprint","IMPRINT",FACE,{"disambiguationData":[TD([[makeQuery(id+"F16.imprint","IMPRINT",EDGE,{"derivedFrom":sQuery(id+"F16.wireOp",EDGE,"E88.MirrorCS")}),-1.0]])]});
            var Q3;
            Q3=makeQuery(id+"F2.opExtrude","CAP_FACE",FACE,{"disambiguationData":[OSD([sQuery(id+"F0.wireOp",EDGE,"E12"),sQuery(id+"F0.wireOp",EDGE,"E13"),sQuery(id+"F0.wireOp",EDGE,"E14"),sQuery(id+"F0.wireOp",EDGE,"E15"),sQuery(id+"F0.wireOp",EDGE,"E17.filletArc"),sQuery(id+"F0.wireOp",EDGE,"E18.filletArc"),sQuery(id+"F0.wireOp",EDGE,"E19.filletArc"),sQuery(id+"F0.wireOp",EDGE,"E20.filletArc"),sQuery(id+"F0.wireOp",EDGE,"E25.0"),sQuery(id+"F0.wireOp",EDGE,"E25.1"),sQuery(id+"F0.wireOp",EDGE,"E25.2"),sQuery(id+"F0.wireOp",EDGE,"E25.3"),sQuery(id+"F0.wireOp",EDGE,"E25.4"),sQuery(id+"F0.wireOp",EDGE,"E25.5"),sQuery(id+"F0.wireOp",EDGE,"E25.6"),sQuery(id+"F0.wireOp",EDGE,"E25.7")])],"isStart":false});
            extrude(context, id + "F17", {"entities" : qUnion([Q0, Q1, Q2]), "endBound" : BoundingType.UP_TO_SURFACE, "depth" : 25 * mm, "endBoundEntityFace" : qUnion([Q3]), "offsetDistance" : 25 * mm});
        }
    });
